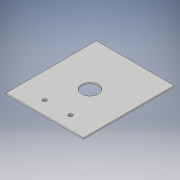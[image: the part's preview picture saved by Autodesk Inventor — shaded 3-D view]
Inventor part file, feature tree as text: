
AUTODESK INVENTOR PART (.ipt)
format: ipt  version: 2019 (Build 230136000, 136)  size: 102,400 bytes
history: native  units: mm
features: extrude x2, sketch x2
ambient origin geometry x8: Origin, YZ Plane, XZ Plane, XY Plane, X Axis, Y Axis, Z Axis, Center Point
bodies: Solid1 (feature_tree)
feature tree (4):
  extrude  "Extrusion1"  Depth=70.0mm
  extrude  "Extrusion2"  Depth=1.0mm
  sketch  "Sketch1"  dims[d0=60.0mm d1=70.0mm]
  sketch  "Sketch2"  dims[d2=1.0mm d3=0.0mm d4=3.0mm d5=3.0mm d6=13.0mm d7=1.0mm d8=0.0mm]
